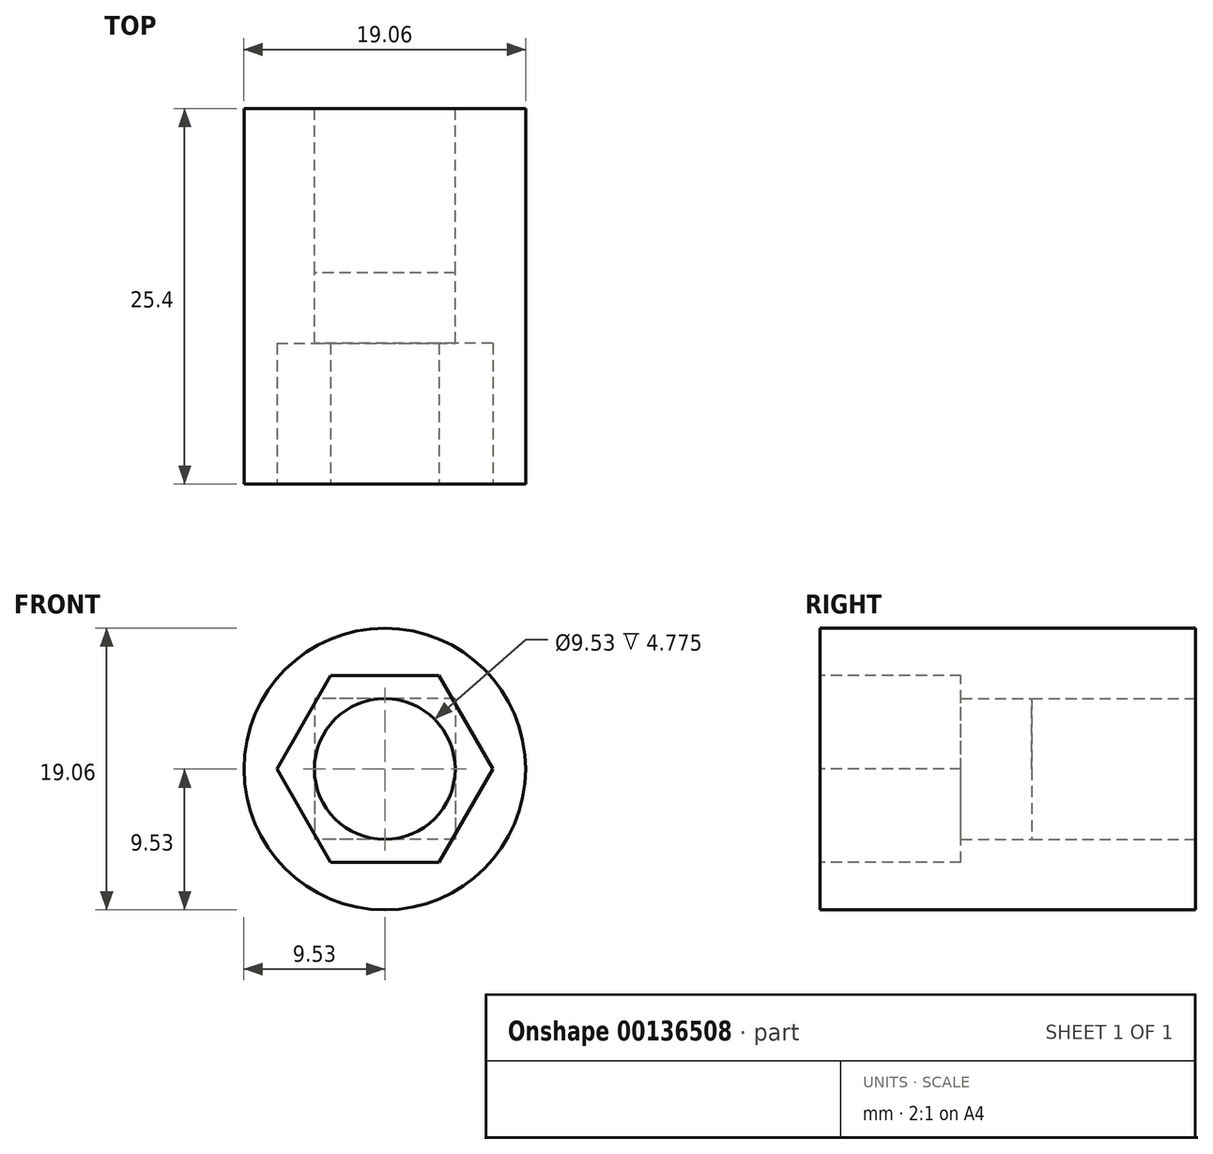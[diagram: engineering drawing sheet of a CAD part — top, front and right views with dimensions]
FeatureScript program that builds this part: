
annotation { "Feature Type Name" : "Feature", "Feature Type Description" : "" }
export const myFeature = defineFeature(function(context is Context, id is Id, definition is map)
    precondition{}
    {
        {
            var Q0;
            Q0=qCreatedBy(makeId("Front.planeOp"),FACE);
            var sketch = newSketch(context, id + "F0", { "sketchPlane" : qUnion([Q0])});
            skCircle(sketch, "E0", {"center": v(0, 0) * mm, "radius": 9.53 * mm});
            skSolve(sketch);
        }
        {
            var Q0;
            Q0 = qSketchRegion(id + "F0", true);
            extrude(context, id + "F1", {"entities" : qUnion([Q0]), "depth" : 25.4 * mm});
        }
        {
            var Q0;
            Q0=qCreatedBy(makeId("Front.planeOp"),FACE);
            var sketch = newSketch(context, id + "F2", { "sketchPlane" : qUnion([Q0])});
            skLineSegment(sketch, "E1.bottom", {"start": v(4.76, 4.76) * mm, "end": v(-4.76, 4.76) * mm});
            skLineSegment(sketch, "E1.top", {"start": v(4.76, -4.76) * mm, "end": v(-4.76, -4.76) * mm});
            skLineSegment(sketch, "E1.left", {"start": v(4.76, 4.76) * mm, "end": v(4.76, -4.76) * mm});
            skLineSegment(sketch, "E1.right", {"start": v(-4.76, 4.76) * mm, "end": v(-4.76, -4.76) * mm});
            skPoint(sketch, "E1.middle", {"position": v(0, 0) * mm});
            skCircle(sketch, "E2", {"center": v(0, 0) * mm, "radius": 4.76 * mm});
            skSolve(sketch);
        }
        {
            var Q0;
            {var subQ0=sQuery(id+"F2.wireOp",EDGE,"E2");var subQ1=makeQuery(id+"F2.imprint","INTERSECT",VERTEX,{"derivedFrom":[sQuery(id+"F2.wireOp",EDGE,"E1.bottom"),subQ0]});Q0=makeQuery(id+"F2.imprint","IMPRINT",FACE,{"disambiguationData":[TD([[makeQuery(id+"F2.imprint","IMPRINT",EDGE,{"disambiguationData":[TD([[subQ1,1.0]])],"derivedFrom":subQ0}),1.0]])]});}
            var Q1;
            Q1=sQuery(id+"F2.wireOp",EDGE,"E2");
            extrude(context, id + "F3", {"entities" : qUnion([Q0]), "operationType" : NewBodyOperationType.REMOVE, "surfaceEntities" : qUnion([Q1]), "endBound" : BoundingType.THROUGH_ALL, "depth" : 25.4 * mm});
        }
        {
            var Q0;
            Q0 = qSketchRegion(id + "F2", true);
            extrude(context, id + "F4", {"entities" : qUnion([Q0]), "operationType" : NewBodyOperationType.REMOVE, "depth" : 11.1 * mm});
        }
        {
            var Q0;
            Q0=makeQuery(id+"F1.opExtrude","CAP_FACE",FACE,{"disambiguationData":[OSD([sQuery(id+"F0.wireOp",EDGE,"E0")])],"isStart":false});
            var sketch = newSketch(context, id + "F5", { "sketchPlane" : qUnion([Q0])});
            skCircle(sketch, "E3.cCircle", {"center": v(0, 0) * mm, "radius": 6.32 * mm, "construction": true});
            skLineSegment(sketch, "E3.0", {"start": v(-3.65, 6.32) * mm, "end": v(3.65, 6.32) * mm});
            skLineSegment(sketch, "E3.1", {"start": v(3.65, 6.32) * mm, "end": v(7.3, 0) * mm});
            skLineSegment(sketch, "E3.2", {"start": v(7.3, 0) * mm, "end": v(3.65, -6.32) * mm});
            skLineSegment(sketch, "E3.3", {"start": v(3.65, -6.32) * mm, "end": v(-3.65, -6.32) * mm});
            skLineSegment(sketch, "E3.4", {"start": v(-3.65, -6.32) * mm, "end": v(-7.3, 0) * mm});
            skLineSegment(sketch, "E3.5", {"start": v(-7.3, 0) * mm, "end": v(-3.65, 6.32) * mm});
            skPoint(sketch, "E3.0.midPoint", {"position": v(0, 6.32) * mm});
            skSolve(sketch);
        }
        {
            var Q0;
            Q0 = qSketchRegion(id + "F5", true);
            extrude(context, id + "F6", {"entities" : qUnion([Q0]), "operationType" : NewBodyOperationType.REMOVE, "oppositeDirection" : true, "depth" : 9.52 * mm});
        }
    });
